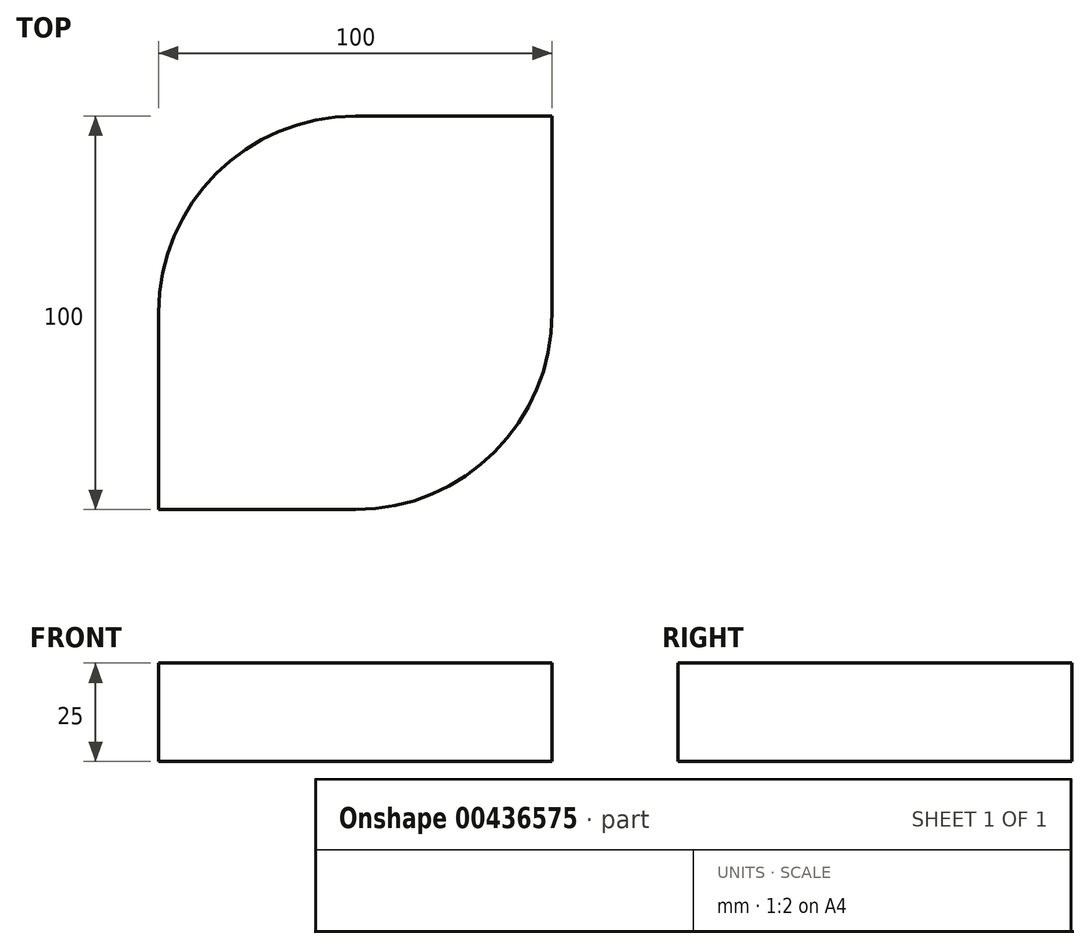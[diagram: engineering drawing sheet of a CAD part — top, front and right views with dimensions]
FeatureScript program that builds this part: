
annotation { "Feature Type Name" : "Feature", "Feature Type Description" : "" }
export const myFeature = defineFeature(function(context is Context, id is Id, definition is map)
    precondition{}
    {
        {
            var Q0;
            Q0=qCreatedBy(makeId("Top.planeOp"),FACE);
            var sketch = newSketch(context, id + "F0", { "sketchPlane" : qUnion([Q0])});
            skArc(sketch, "E0", {"start": v(0, 50) * mm, "mid": v(-35.36, 35.36) * mm, "end": v(-50, 0) * mm});
            skLineSegment(sketch, "E1.bottom", {"start": v(0, -50) * mm, "end": v(-50, -50) * mm});
            skLineSegment(sketch, "E1.top", {"start": v(50, 50) * mm, "end": v(0, 50) * mm});
            skLineSegment(sketch, "E1.left", {"start": v(50, 0) * mm, "end": v(50, 50) * mm});
            skLineSegment(sketch, "E1.right", {"start": v(-50, -50) * mm, "end": v(-50, 0) * mm});
            skPoint(sketch, "E2.orphan", {"position": v(-50, 50) * mm});
            skPoint(sketch, "E3.orphan", {"position": v(50, -50) * mm});
            skArc(sketch, "E4.trimOffspring", {"start": v(0, -50) * mm, "mid": v(35.36, -35.36) * mm, "end": v(50, 0) * mm});
            skSolve(sketch);
        }
        {
            var Q0;
            Q0 = qSketchRegion(id + "F0", true);
            extrude(context, id + "F1", {"entities" : qUnion([Q0]), "depth" : 25 * mm});
        }
    });
